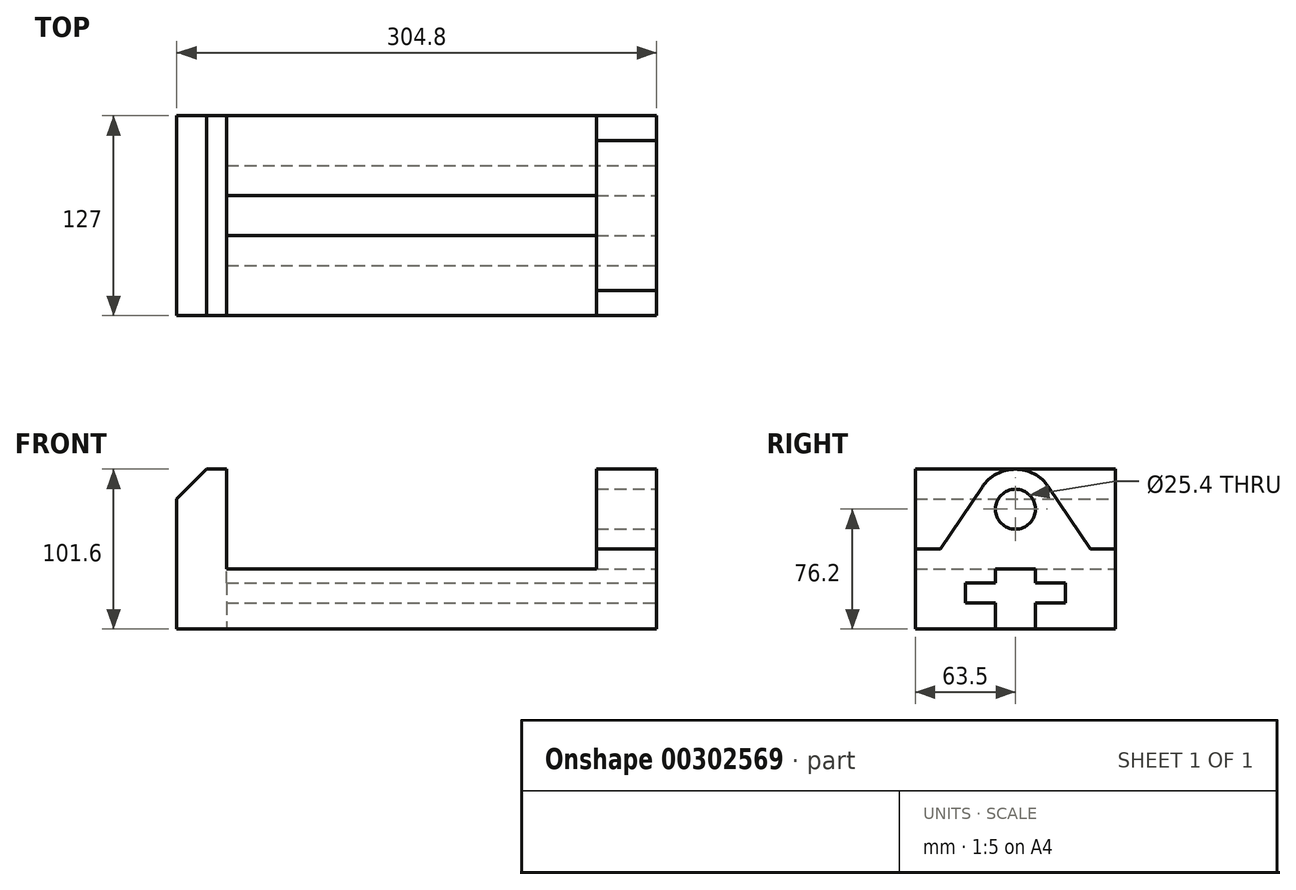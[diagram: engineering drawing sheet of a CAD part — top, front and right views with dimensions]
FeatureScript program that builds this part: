
annotation { "Feature Type Name" : "Feature", "Feature Type Description" : "" }
export const myFeature = defineFeature(function(context is Context, id is Id, definition is map)
    precondition{}
    {
        {
            var Q0;
            Q0=qCreatedBy(makeId("Front.planeOp"),FACE);
            var sketch = newSketch(context, id + "F0", { "sketchPlane" : qUnion([Q0])});
            skLineSegment(sketch, "E0", {"start": v(0, 0) * mm, "end": v(-304.8, 0) * mm});
            skLineSegment(sketch, "E1", {"start": v(-304.8, 0) * mm, "end": v(-304.8, 82.55) * mm});
            skLineSegment(sketch, "E2", {"start": v(-304.8, 82.55) * mm, "end": v(-285.75, 101.6) * mm});
            skLineSegment(sketch, "E3", {"start": v(-285.75, 101.6) * mm, "end": v(-273.05, 101.6) * mm});
            skLineSegment(sketch, "E4", {"start": v(-273.05, 101.6) * mm, "end": v(-273.05, 38.1) * mm});
            skLineSegment(sketch, "E5", {"start": v(-273.05, 38.1) * mm, "end": v(-38.1, 38.1) * mm});
            skLineSegment(sketch, "E6", {"start": v(-38.1, 38.1) * mm, "end": v(-38.1, 101.6) * mm});
            skLineSegment(sketch, "E7", {"start": v(-38.1, 101.6) * mm, "end": v(0, 101.6) * mm});
            skLineSegment(sketch, "E8", {"start": v(0, 101.6) * mm, "end": v(0, 0) * mm});
            skLineSegment(sketch, "E9", {"start": v(-304.8, 82.55) * mm, "end": v(-304.8, 101.6) * mm, "construction": true});
            skLineSegment(sketch, "E10", {"start": v(-304.8, 101.6) * mm, "end": v(-285.75, 101.6) * mm, "construction": true});
            skSolve(sketch);
        }
        {
            var Q0;
            Q0=makeQuery(id+"F0.imprint","IMPRINT",FACE,{"disambiguationData":[TD([[makeQuery(id+"F0.imprint","IMPRINT",EDGE,{"derivedFrom":sQuery(id+"F0.wireOp",EDGE,"E0")}),-1.0]])]});
            extrude(context, id + "F1", {"entities" : qUnion([Q0]), "endBound" : BoundingType.SYMMETRIC, "depth" : 127 * mm});
        }
        {
            var Q0;
            Q0=makeQuery(id+"F1.opExtrude","SWEPT_FACE",FACE,{"disambiguationData":[OSD([sQuery(id+"F0.wireOp",EDGE,"E8")])]});
            var sketch = newSketch(context, id + "F2", { "sketchPlane" : qUnion([Q0])});
            skLineSegment(sketch, "E11", {"start": v(0, 101.6) * mm, "end": v(0, 0) * mm, "construction": true});
            skLineSegment(sketch, "E12", {"start": v(-63.5, 0) * mm, "end": v(0, 0) * mm});
            skLineSegment(sketch, "E13", {"start": v(-63.5, 0) * mm, "end": v(-63.5, 50.8) * mm});
            skLineSegment(sketch, "E14", {"start": v(-63.5, 50.8) * mm, "end": v(-47.63, 50.8) * mm});
            skLineSegment(sketch, "E15", {"start": v(-47.63, 50.8) * mm, "end": v(-21.1, 90.35) * mm});
            skCircle(sketch, "E16", {"center": v(0, 76.2) * mm, "radius": 12.7 * mm});
            skLineSegment(sketch, "E17.bottom", {"start": v(-12.7, 0) * mm, "end": v(12.7, 0) * mm, "construction": true});
            skLineSegment(sketch, "E17.top", {"start": v(-12.7, 38.1) * mm, "end": v(12.7, 38.1) * mm, "construction": true});
            skLineSegment(sketch, "E17.left", {"start": v(-12.7, 0) * mm, "end": v(-12.7, 38.1) * mm, "construction": true});
            skLineSegment(sketch, "E17.right", {"start": v(12.7, 0) * mm, "end": v(12.7, 38.1) * mm, "construction": true});
            skLineSegment(sketch, "E18", {"start": v(-12.7, 0) * mm, "end": v(-12.7, 16.51) * mm});
            skLineSegment(sketch, "E19", {"start": v(-12.7, 16.51) * mm, "end": v(-31.75, 16.51) * mm});
            skLineSegment(sketch, "E20", {"start": v(-31.75, 16.51) * mm, "end": v(-31.75, 29.2) * mm});
            skLineSegment(sketch, "E21", {"start": v(-31.75, 29.21) * mm, "end": v(-12.7, 29.21) * mm});
            skLineSegment(sketch, "E22.MirrorCS", {"start": v(31.75, 29.21) * mm, "end": v(12.7, 29.21) * mm});
            skLineSegment(sketch, "E23.MirrorCS", {"start": v(12.7, 16.51) * mm, "end": v(31.75, 16.51) * mm});
            skLineSegment(sketch, "E24.MirrorCS", {"start": v(31.75, 16.51) * mm, "end": v(31.75, 29.21) * mm});
            skLineSegment(sketch, "E25", {"start": v(-12.7, 38.1) * mm, "end": v(12.7, 38.1) * mm});
            skLineSegment(sketch, "E26.MirrorCS", {"start": v(47.63, 50.8) * mm, "end": v(21.1, 90.35) * mm});
            skLineSegment(sketch, "E27.MirrorCS", {"start": v(63.5, 50.8) * mm, "end": v(47.63, 50.8) * mm});
            skLineSegment(sketch, "E28.MirrorCS", {"start": v(63.5, 0) * mm, "end": v(63.5, 50.8) * mm});
            skLineSegment(sketch, "E29.MirrorCS", {"start": v(63.5, 0) * mm, "end": v(0, 0) * mm});
            skArc(sketch, "E30", {"start": v(21.1, 90.35) * mm, "mid": v(0, 101.6) * mm, "end": v(-21.1, 90.35) * mm});
            skLineSegment(sketch, "E31", {"start": v(12.7, 16.51) * mm, "end": v(12.7, 0) * mm});
            skLineSegment(sketch, "E32", {"start": v(12.7, 29.21) * mm, "end": v(12.7, 38.1) * mm});
            skLineSegment(sketch, "E33", {"start": v(-12.7, 38.1) * mm, "end": v(-12.7, 29.21) * mm});
            skSolve(sketch);
        }
        {
            var Q0;
            {var subQ7=sQuery(id+"F2.wireOp",EDGE,"E14");Q0=makeQuery(id+"F2.imprint","IMPRINT",FACE,{"disambiguationData":[TD([[makeQuery(id+"F2.imprint","IMPRINT",EDGE,{"derivedFrom":subQ7}),1.0]])]});}
            var Q1;
            {var subQ1=sQuery(id+"F2.wireOp",EDGE,"E26.MirrorCS");Q1=makeQuery(id+"F2.imprint","IMPRINT",FACE,{"disambiguationData":[TD([[makeQuery(id+"F2.imprint","IMPRINT",EDGE,{"derivedFrom":subQ1}),-1.0]])]});}
            var Q2;
            Q2=makeQuery(id+"F1.opExtrude","SWEPT_FACE",FACE,{"disambiguationData":[OSD([sQuery(id+"F0.wireOp",EDGE,"E6")])]});
            extrude(context, id + "F3", {"entities" : qUnion([Q0, Q1]), "operationType" : NewBodyOperationType.REMOVE, "endBound" : BoundingType.UP_TO_SURFACE, "oppositeDirection" : true, "endBoundEntityFace" : qUnion([Q2]), "depth" : 25.4 * mm});
        }
        {
            var Q0;
            Q0=makeQuery(id+"F2.imprint","IMPRINT",FACE,{"disambiguationData":[TD([[makeQuery(id+"F2.imprint","IMPRINT",EDGE,{"derivedFrom":sQuery(id+"F2.wireOp",EDGE,"E16")}),1.0]])]});
            var Q1;
            Q1=makeQuery(id+"F1.opExtrude","SWEPT_FACE",FACE,{"disambiguationData":[OSD([sQuery(id+"F0.wireOp",EDGE,"E6")])]});
            extrude(context, id + "F4", {"entities" : qUnion([Q0]), "operationType" : NewBodyOperationType.REMOVE, "endBound" : BoundingType.UP_TO_SURFACE, "oppositeDirection" : true, "endBoundEntityFace" : qUnion([Q1]), "depth" : 25.4 * mm});
        }
        {
            var Q0;
            {var subQ3=sQuery(id+"F2.wireOp",EDGE,"E18");Q0=makeQuery(id+"F2.imprint","IMPRINT",FACE,{"disambiguationData":[TD([[makeQuery(id+"F2.imprint","IMPRINT",EDGE,{"derivedFrom":subQ3}),-1.0]])]});}
            var Q1;
            Q1=makeQuery(id+"F1.opExtrude","SWEPT_FACE",FACE,{"disambiguationData":[OSD([sQuery(id+"F0.wireOp",EDGE,"E4")])]});
            extrude(context, id + "F5", {"entities" : qUnion([Q0]), "operationType" : NewBodyOperationType.REMOVE, "endBound" : BoundingType.UP_TO_SURFACE, "oppositeDirection" : true, "endBoundEntityFace" : qUnion([Q1]), "depth" : 25.4 * mm});
        }
    });
